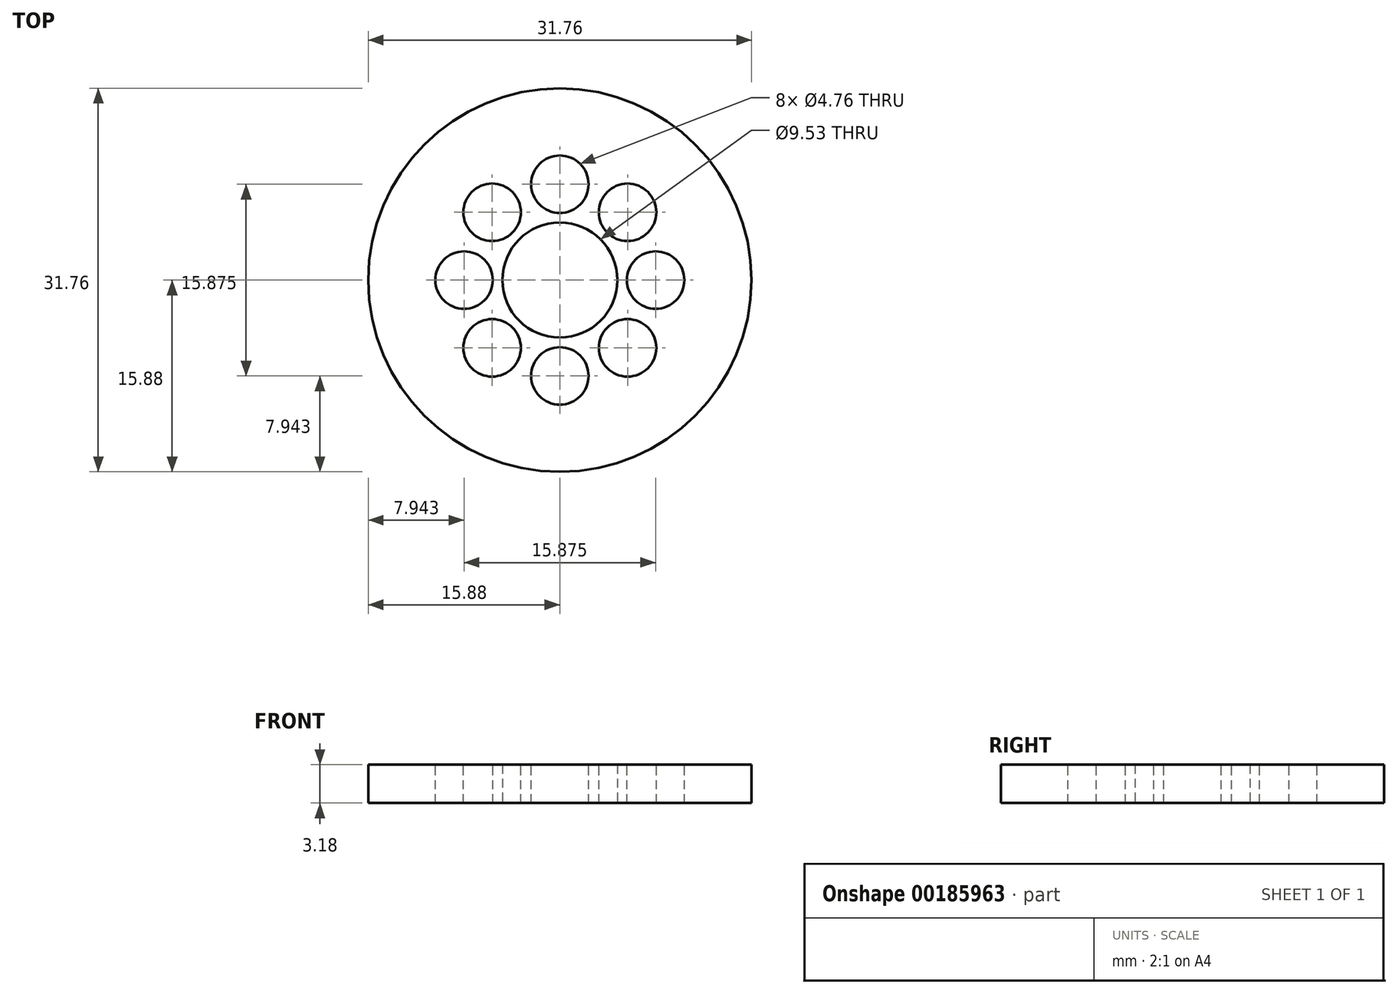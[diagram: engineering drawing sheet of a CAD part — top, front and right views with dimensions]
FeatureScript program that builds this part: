
annotation { "Feature Type Name" : "Feature", "Feature Type Description" : "" }
export const myFeature = defineFeature(function(context is Context, id is Id, definition is map)
    precondition{}
    {
        {
            var Q0;
            Q0=qCreatedBy(makeId("Top.planeOp"),FACE);
            var sketch = newSketch(context, id + "F0", { "sketchPlane" : qUnion([Q0])});
            skCircle(sketch, "E0", {"center": v(0, 0) * mm, "radius": 15.88 * mm});
            skCircle(sketch, "E1", {"center": v(0, 0) * mm, "radius": 4.76 * mm});
            skSolve(sketch);
        }
        {
            var Q0;
            Q0=qSketchRegion(id+"F0",true);
            extrude(context, id + "F1", {"entities" : qUnion([Q0]), "depth" : 3.17 * mm});
        }
        {
            var Q0;
            Q0=makeQuery(id+"F1.opExtrude","CAP_FACE",FACE,{"disambiguationData":[OSD([sQuery(id+"F0.wireOp",EDGE,"E0"),sQuery(id+"F0.wireOp",EDGE,"E1")])],"isStart":false});
            var sketch = newSketch(context, id + "F2", { "sketchPlane" : qUnion([Q0])});
            skCircle(sketch, "E2", {"center": v(0, 0) * mm, "radius": 4.76 * mm});
            skLineSegment(sketch, "E3.bottom", {"start": v(-2.38, 6.35) * mm, "end": v(2.38, 6.35) * mm});
            skLineSegment(sketch, "E3.top", {"start": v(-2.38, -6.35) * mm, "end": v(2.38, -6.35) * mm});
            skLineSegment(sketch, "E3.left", {"start": v(-2.38, 6.35) * mm, "end": v(-2.38, -6.35) * mm});
            skLineSegment(sketch, "E3.right", {"start": v(2.38, 6.35) * mm, "end": v(2.38, -6.35) * mm});
            skLineSegment(sketch, "E4.bottom", {"start": v(-6.35, 2.38) * mm, "end": v(6.35, 2.38) * mm});
            skLineSegment(sketch, "E4.top", {"start": v(-6.35, -2.38) * mm, "end": v(6.35, -2.38) * mm});
            skLineSegment(sketch, "E4.left", {"start": v(-6.35, 2.38) * mm, "end": v(-6.35, -2.38) * mm});
            skLineSegment(sketch, "E4.right", {"start": v(6.35, 2.38) * mm, "end": v(6.35, -2.38) * mm});
            skCircle(sketch, "E5", {"center": v(0, 0) * mm, "radius": 5.72 * mm});
            skSolve(sketch);
        }
        {
            var Q0;
            {var subQ5=sQuery(id+"F2.wireOp",EDGE,"E3.bottom");Q0=makeQuery(id+"F2.imprint","IMPRINT",FACE,{"disambiguationData":[TD([[makeQuery(id+"F2.imprint","IMPRINT",EDGE,{"derivedFrom":subQ5}),-1.0]])]});}
            var Q1;
            {var subQ5=sQuery(id+"F2.wireOp",EDGE,"E3.top");Q1=makeQuery(id+"F2.imprint","IMPRINT",FACE,{"disambiguationData":[TD([[makeQuery(id+"F2.imprint","IMPRINT",EDGE,{"derivedFrom":subQ5}),1.0]])]});}
            var Q2;
            {var subQ5=sQuery(id+"F2.wireOp",EDGE,"E4.right");Q2=makeQuery(id+"F2.imprint","IMPRINT",FACE,{"disambiguationData":[TD([[makeQuery(id+"F2.imprint","IMPRINT",EDGE,{"derivedFrom":subQ5}),-1.0]])]});}
            var Q3;
            {var subQ0=sQuery(id+"F2.wireOp",EDGE,"E3.left");var subQ1=sQuery(id+"F2.wireOp",EDGE,"E2");var subQ2=makeQuery(id+"F2.imprint","INTERSECT",VERTEX,{"disambiguationData":[OD(0.0)],"derivedFrom":[subQ1,subQ0]});Q3=makeQuery(id+"F2.imprint","IMPRINT",FACE,{"disambiguationData":[TD([[makeQuery(id+"F2.imprint","IMPRINT",EDGE,{"disambiguationData":[TD([[subQ2,-1.0]])],"derivedFrom":subQ1}),-1.0]])]});}
            var Q4;
            {var subQ0=sQuery(id+"F2.wireOp",EDGE,"E3.right");var subQ1=sQuery(id+"F2.wireOp",EDGE,"E2");var subQ2=makeQuery(id+"F2.imprint","INTERSECT",VERTEX,{"disambiguationData":[OD(0.0)],"derivedFrom":[subQ1,subQ0]});Q4=makeQuery(id+"F2.imprint","IMPRINT",FACE,{"disambiguationData":[TD([[makeQuery(id+"F2.imprint","IMPRINT",EDGE,{"disambiguationData":[TD([[subQ2,-1.0]])],"derivedFrom":subQ1}),-1.0]])]});}
            var Q5;
            {var subQ0=sQuery(id+"F2.wireOp",EDGE,"E3.right");var subQ1=sQuery(id+"F2.wireOp",EDGE,"E2");var subQ2=makeQuery(id+"F2.imprint","INTERSECT",VERTEX,{"disambiguationData":[OD(0.0)],"derivedFrom":[subQ1,subQ0]});Q5=makeQuery(id+"F2.imprint","IMPRINT",FACE,{"disambiguationData":[TD([[makeQuery(id+"F2.imprint","IMPRINT",EDGE,{"disambiguationData":[TD([[subQ2,1.0]])],"derivedFrom":subQ1}),-1.0]])]});}
            var Q6;
            {var subQ0=sQuery(id+"F2.wireOp",EDGE,"E4.bottom");var subQ1=sQuery(id+"F2.wireOp",EDGE,"E2");var subQ2=makeQuery(id+"F2.imprint","INTERSECT",VERTEX,{"disambiguationData":[OD(0.0)],"derivedFrom":[subQ1,subQ0]});Q6=makeQuery(id+"F2.imprint","IMPRINT",FACE,{"disambiguationData":[TD([[makeQuery(id+"F2.imprint","IMPRINT",EDGE,{"disambiguationData":[TD([[subQ2,1.0]])],"derivedFrom":subQ1}),-1.0]])]});}
            var Q7;
            {var subQ0=sQuery(id+"F2.wireOp",EDGE,"E3.right");var subQ1=sQuery(id+"F2.wireOp",EDGE,"E2");var subQ2=makeQuery(id+"F2.imprint","INTERSECT",VERTEX,{"disambiguationData":[OD(1.0)],"derivedFrom":[subQ1,subQ0]});Q7=makeQuery(id+"F2.imprint","IMPRINT",FACE,{"disambiguationData":[TD([[makeQuery(id+"F2.imprint","IMPRINT",EDGE,{"disambiguationData":[TD([[subQ2,-1.0]])],"derivedFrom":subQ1}),-1.0]])]});}
            var Q8;
            {var subQ0=sQuery(id+"F2.wireOp",EDGE,"E3.left");var subQ1=sQuery(id+"F2.wireOp",EDGE,"E2");var subQ2=makeQuery(id+"F2.imprint","INTERSECT",VERTEX,{"disambiguationData":[OD(1.0)],"derivedFrom":[subQ1,subQ0]});Q8=makeQuery(id+"F2.imprint","IMPRINT",FACE,{"disambiguationData":[TD([[makeQuery(id+"F2.imprint","IMPRINT",EDGE,{"disambiguationData":[TD([[subQ2,-1.0]])],"derivedFrom":subQ1}),-1.0]])]});}
            var Q9;
            {var subQ0=sQuery(id+"F2.wireOp",EDGE,"E4.top");var subQ1=sQuery(id+"F2.wireOp",EDGE,"E2");var subQ2=makeQuery(id+"F2.imprint","INTERSECT",VERTEX,{"disambiguationData":[OD(0.0)],"derivedFrom":[subQ1,subQ0]});Q9=makeQuery(id+"F2.imprint","IMPRINT",FACE,{"disambiguationData":[TD([[makeQuery(id+"F2.imprint","IMPRINT",EDGE,{"disambiguationData":[TD([[subQ2,-1.0]])],"derivedFrom":subQ1}),-1.0]])]});}
            var Q10;
            {var subQ0=sQuery(id+"F2.wireOp",EDGE,"E4.bottom");var subQ1=sQuery(id+"F2.wireOp",EDGE,"E2");var subQ2=makeQuery(id+"F2.imprint","INTERSECT",VERTEX,{"disambiguationData":[OD(1.0)],"derivedFrom":[subQ1,subQ0]});Q10=makeQuery(id+"F2.imprint","IMPRINT",FACE,{"disambiguationData":[TD([[makeQuery(id+"F2.imprint","IMPRINT",EDGE,{"disambiguationData":[TD([[subQ2,-1.0]])],"derivedFrom":subQ1}),-1.0]])]});}
            var Q11;
            {var subQ0=sQuery(id+"F2.wireOp",EDGE,"E4.left");Q11=makeQuery(id+"F2.imprint","IMPRINT",FACE,{"disambiguationData":[TD([[makeQuery(id+"F2.imprint","IMPRINT",EDGE,{"derivedFrom":subQ0}),1.0]])]});}
            extrude(context, id + "F3", {"entities" : qUnion([Q0, Q1, Q2, Q3, Q4, Q5, Q6, Q7, Q8, Q9, Q10, Q11]), "depth" : 6.35 * mm});
        }
        {
            var Q0;
            Q0=makeQuery(id+"F3.opExtrude","CAP_FACE",FACE,{"disambiguationData":[OSD([sQuery(id+"F2.wireOp",EDGE,"E2"),sQuery(id+"F2.wireOp",EDGE,"E3.bottom"),sQuery(id+"F2.wireOp",EDGE,"E3.top"),sQuery(id+"F2.wireOp",EDGE,"E3.left"),sQuery(id+"F2.wireOp",EDGE,"E3.right"),sQuery(id+"F2.wireOp",EDGE,"E4.bottom"),sQuery(id+"F2.wireOp",EDGE,"E4.top"),sQuery(id+"F2.wireOp",EDGE,"E4.left"),sQuery(id+"F2.wireOp",EDGE,"E4.right")])],"isStart":false});
            var sketch = newSketch(context, id + "F4", { "sketchPlane" : qUnion([Q0])});
            skCircle(sketch, "E6", {"center": v(0, 0) * mm, "radius": 15.88 * mm});
            skCircle(sketch, "E7", {"center": v(0, 0) * mm, "radius": 4.76 * mm});
            skSolve(sketch);
        }
        {
            var Q0;
            Q0=qSketchRegion(id+"F4",true);
            extrude(context, id + "F5", {"entities" : qUnion([Q0]), "operationType" : NewBodyOperationType.ADD, "depth" : 3.17 * mm});
        }
        {
            var Q0;
            Q0=makeQuery(id+"F5.opExtrude","CAP_FACE",FACE,{"disambiguationData":[OSD([sQuery(id+"F4.wireOp",EDGE,"E6"),sQuery(id+"F4.wireOp",EDGE,"E7")])],"isStart":false});
            var sketch = newSketch(context, id + "F6", { "sketchPlane" : qUnion([Q0])});
            skCircle(sketch, "E8", {"center": v(0, 7.94) * mm, "radius": 2.38 * mm});
            skCircle(sketch, "E9.1.0", {"center": v(-5.61, 5.61) * mm, "radius": 2.38 * mm});
            skCircle(sketch, "E9.2.0", {"center": v(-7.94, 0) * mm, "radius": 2.38 * mm});
            skCircle(sketch, "E9.3.0", {"center": v(-5.61, -5.61) * mm, "radius": 2.38 * mm});
            skCircle(sketch, "E9.4.0", {"center": v(0, -7.94) * mm, "radius": 2.38 * mm});
            skCircle(sketch, "E9.5.0", {"center": v(5.61, -5.61) * mm, "radius": 2.38 * mm});
            skCircle(sketch, "E9.6.0", {"center": v(7.94, 0) * mm, "radius": 2.38 * mm});
            skCircle(sketch, "E9.7.0", {"center": v(5.61, 5.61) * mm, "radius": 2.38 * mm});
            skPoint(sketch, "E9.center", {"position": v(0, 0) * mm});
            skSolve(sketch);
        }
        {
            var Q0;
            Q0=makeQuery(id+"F6.imprint","IMPRINT",FACE,{"disambiguationData":[TD([[makeQuery(id+"F6.imprint","IMPRINT",EDGE,{"derivedFrom":sQuery(id+"F6.wireOp",EDGE,"E9.1.0")}),1.0]])]});
            var Q1;
            Q1=makeQuery(id+"F6.imprint","IMPRINT",FACE,{"disambiguationData":[TD([[makeQuery(id+"F6.imprint","IMPRINT",EDGE,{"derivedFrom":sQuery(id+"F6.wireOp",EDGE,"E9.5.0")}),1.0]])]});
            var Q2;
            Q2=makeQuery(id+"F6.imprint","IMPRINT",FACE,{"disambiguationData":[TD([[makeQuery(id+"F6.imprint","IMPRINT",EDGE,{"derivedFrom":sQuery(id+"F6.wireOp",EDGE,"E8")}),1.0]])]});
            var Q3;
            Q3=makeQuery(id+"F6.imprint","IMPRINT",FACE,{"disambiguationData":[TD([[makeQuery(id+"F6.imprint","IMPRINT",EDGE,{"derivedFrom":sQuery(id+"F6.wireOp",EDGE,"E9.7.0")}),1.0]])]});
            var Q4;
            Q4=makeQuery(id+"F6.imprint","IMPRINT",FACE,{"disambiguationData":[TD([[makeQuery(id+"F6.imprint","IMPRINT",EDGE,{"derivedFrom":sQuery(id+"F6.wireOp",EDGE,"E9.6.0")}),1.0]])]});
            var Q5;
            Q5=makeQuery(id+"F6.imprint","IMPRINT",FACE,{"disambiguationData":[TD([[makeQuery(id+"F6.imprint","IMPRINT",EDGE,{"derivedFrom":sQuery(id+"F6.wireOp",EDGE,"E9.4.0")}),1.0]])]});
            var Q6;
            Q6=makeQuery(id+"F6.imprint","IMPRINT",FACE,{"disambiguationData":[TD([[makeQuery(id+"F6.imprint","IMPRINT",EDGE,{"derivedFrom":sQuery(id+"F6.wireOp",EDGE,"E9.3.0")}),1.0]])]});
            var Q7;
            Q7=makeQuery(id+"F6.imprint","IMPRINT",FACE,{"disambiguationData":[TD([[makeQuery(id+"F6.imprint","IMPRINT",EDGE,{"derivedFrom":sQuery(id+"F6.wireOp",EDGE,"E9.2.0")}),1.0]])]});
            extrude(context, id + "F7", {"entities" : qUnion([Q0, Q1, Q2, Q3, Q4, Q5, Q6, Q7]), "operationType" : NewBodyOperationType.REMOVE, "oppositeDirection" : true, "depth" : 25.4 * mm});
        }
        {
            var Q0;
            Q0=makeQuery(id+"F1.opExtrude","CAP_FACE",FACE,{"disambiguationData":[OSD([sQuery(id+"F0.wireOp",EDGE,"E0"),sQuery(id+"F0.wireOp",EDGE,"E1")])],"isStart":true});
            var sketch = newSketch(context, id + "F8", { "sketchPlane" : qUnion([Q0])});
            skCircle(sketch, "E10", {"center": v(0, 7.94) * mm, "radius": 1.59 * mm});
            skCircle(sketch, "E11.1.0", {"center": v(-5.61, 5.61) * mm, "radius": 1.59 * mm});
            skCircle(sketch, "E11.2.0", {"center": v(-7.94, 0) * mm, "radius": 1.59 * mm});
            skCircle(sketch, "E11.3.0", {"center": v(-5.61, -5.61) * mm, "radius": 1.59 * mm});
            skCircle(sketch, "E11.4.0", {"center": v(0, -7.94) * mm, "radius": 1.59 * mm});
            skCircle(sketch, "E11.5.0", {"center": v(5.61, -5.61) * mm, "radius": 1.59 * mm});
            skCircle(sketch, "E11.6.0", {"center": v(7.94, 0) * mm, "radius": 1.59 * mm});
            skCircle(sketch, "E11.7.0", {"center": v(5.61, 5.61) * mm, "radius": 1.59 * mm});
            skPoint(sketch, "E11.center", {"position": v(0, 0) * mm});
            skSolve(sketch);
        }
        {
            var Q0;
            Q0=makeQuery(id+"F8.imprint","IMPRINT",FACE,{"disambiguationData":[TD([[makeQuery(id+"F8.imprint","IMPRINT",EDGE,{"derivedFrom":sQuery(id+"F8.wireOp",EDGE,"E10")}),-1.0]])]});
            var Q1;
            Q1=makeQuery(id+"F8.imprint","IMPRINT",FACE,{"disambiguationData":[TD([[makeQuery(id+"F8.imprint","IMPRINT",EDGE,{"derivedFrom":sQuery(id+"F8.wireOp",EDGE,"E11.7.0")}),-1.0]])]});
            var Q2;
            Q2=makeQuery(id+"F8.imprint","IMPRINT",FACE,{"disambiguationData":[TD([[makeQuery(id+"F8.imprint","IMPRINT",EDGE,{"derivedFrom":sQuery(id+"F8.wireOp",EDGE,"E11.6.0")}),-1.0]])]});
            var Q3;
            Q3=makeQuery(id+"F8.imprint","IMPRINT",FACE,{"disambiguationData":[TD([[makeQuery(id+"F8.imprint","IMPRINT",EDGE,{"derivedFrom":sQuery(id+"F8.wireOp",EDGE,"E11.5.0")}),-1.0]])]});
            var Q4;
            Q4=makeQuery(id+"F8.imprint","IMPRINT",FACE,{"disambiguationData":[TD([[makeQuery(id+"F8.imprint","IMPRINT",EDGE,{"derivedFrom":sQuery(id+"F8.wireOp",EDGE,"E11.4.0")}),-1.0]])]});
            var Q5;
            Q5=makeQuery(id+"F8.imprint","IMPRINT",FACE,{"disambiguationData":[TD([[makeQuery(id+"F8.imprint","IMPRINT",EDGE,{"derivedFrom":sQuery(id+"F8.wireOp",EDGE,"E11.3.0")}),-1.0]])]});
            var Q6;
            Q6=makeQuery(id+"F8.imprint","IMPRINT",FACE,{"disambiguationData":[TD([[makeQuery(id+"F8.imprint","IMPRINT",EDGE,{"derivedFrom":sQuery(id+"F8.wireOp",EDGE,"E11.2.0")}),-1.0]])]});
            var Q7;
            Q7=makeQuery(id+"F8.imprint","IMPRINT",FACE,{"disambiguationData":[TD([[makeQuery(id+"F8.imprint","IMPRINT",EDGE,{"derivedFrom":sQuery(id+"F8.wireOp",EDGE,"E11.1.0")}),-1.0]])]});
            var Q8;
            Q8=makeQuery(id+"F8.imprint","IMPRINT",FACE,{"disambiguationData":[TD([[makeQuery(id+"F8.imprint","IMPRINT",EDGE,{"derivedFrom":sQuery(id+"F8.wireOp",EDGE,"E11.6.0")}),1.0]])]});
            var Q9;
            Q9=makeQuery(id+"F8.imprint","IMPRINT",FACE,{"disambiguationData":[TD([[makeQuery(id+"F8.imprint","IMPRINT",EDGE,{"derivedFrom":sQuery(id+"F8.wireOp",EDGE,"E11.5.0")}),1.0]])]});
            var Q10;
            Q10=makeQuery(id+"F8.imprint","IMPRINT",FACE,{"disambiguationData":[TD([[makeQuery(id+"F8.imprint","IMPRINT",EDGE,{"derivedFrom":sQuery(id+"F8.wireOp",EDGE,"E11.4.0")}),1.0]])]});
            var Q11;
            Q11=makeQuery(id+"F8.imprint","IMPRINT",FACE,{"disambiguationData":[TD([[makeQuery(id+"F8.imprint","IMPRINT",EDGE,{"derivedFrom":sQuery(id+"F8.wireOp",EDGE,"E11.3.0")}),1.0]])]});
            var Q12;
            Q12=makeQuery(id+"F8.imprint","IMPRINT",FACE,{"disambiguationData":[TD([[makeQuery(id+"F8.imprint","IMPRINT",EDGE,{"derivedFrom":sQuery(id+"F8.wireOp",EDGE,"E11.2.0")}),1.0]])]});
            var Q13;
            Q13=makeQuery(id+"F8.imprint","IMPRINT",FACE,{"disambiguationData":[TD([[makeQuery(id+"F8.imprint","IMPRINT",EDGE,{"derivedFrom":sQuery(id+"F8.wireOp",EDGE,"E11.1.0")}),1.0]])]});
            var Q14;
            Q14=makeQuery(id+"F8.imprint","IMPRINT",FACE,{"disambiguationData":[TD([[makeQuery(id+"F8.imprint","IMPRINT",EDGE,{"derivedFrom":sQuery(id+"F8.wireOp",EDGE,"E10")}),1.0]])]});
            var Q15;
            Q15=makeQuery(id+"F8.imprint","IMPRINT",FACE,{"disambiguationData":[TD([[makeQuery(id+"F8.imprint","IMPRINT",EDGE,{"derivedFrom":sQuery(id+"F8.wireOp",EDGE,"E11.7.0")}),1.0]])]});
            extrude(context, id + "F9", {"entities" : qUnion([Q0, Q1, Q2, Q3, Q4, Q5, Q6, Q7, Q8, Q9, Q10, Q11, Q12, Q13, Q14, Q15]), "operationType" : NewBodyOperationType.REMOVE, "oppositeDirection" : true, "depth" : 25.4 * mm});
        }
        {
            var Q0;
            Q0=makeQuery(id+"F5.opExtrude","CAP_FACE",FACE,{"disambiguationData":[OSD([sQuery(id+"F4.wireOp",EDGE,"E6"),sQuery(id+"F4.wireOp",EDGE,"E7")])],"isStart":false});
            extrude(context, id + "F10", {"entities" : qUnion([Q0]), "operationType" : NewBodyOperationType.REMOVE, "oppositeDirection" : true, "depth" : 3.17 * mm});
        }
        {
            var Q0;
            Q0=makeQuery(id+"F10.boolean.opBoolean","COPY",FACE,{"derivedFrom":makeQuery(id+"F10.opExtrude","CAP_FACE",FACE,{"disambiguationData":[OSD([sQuery(id+"F4.wireOp",EDGE,"E6"),sQuery(id+"F4.wireOp",EDGE,"E7")])],"isStart":false})});
            extrude(context, id + "F11", {"entities" : qUnion([Q0]), "operationType" : NewBodyOperationType.REMOVE, "oppositeDirection" : true, "depth" : 6.35 * mm});
        }
    });
